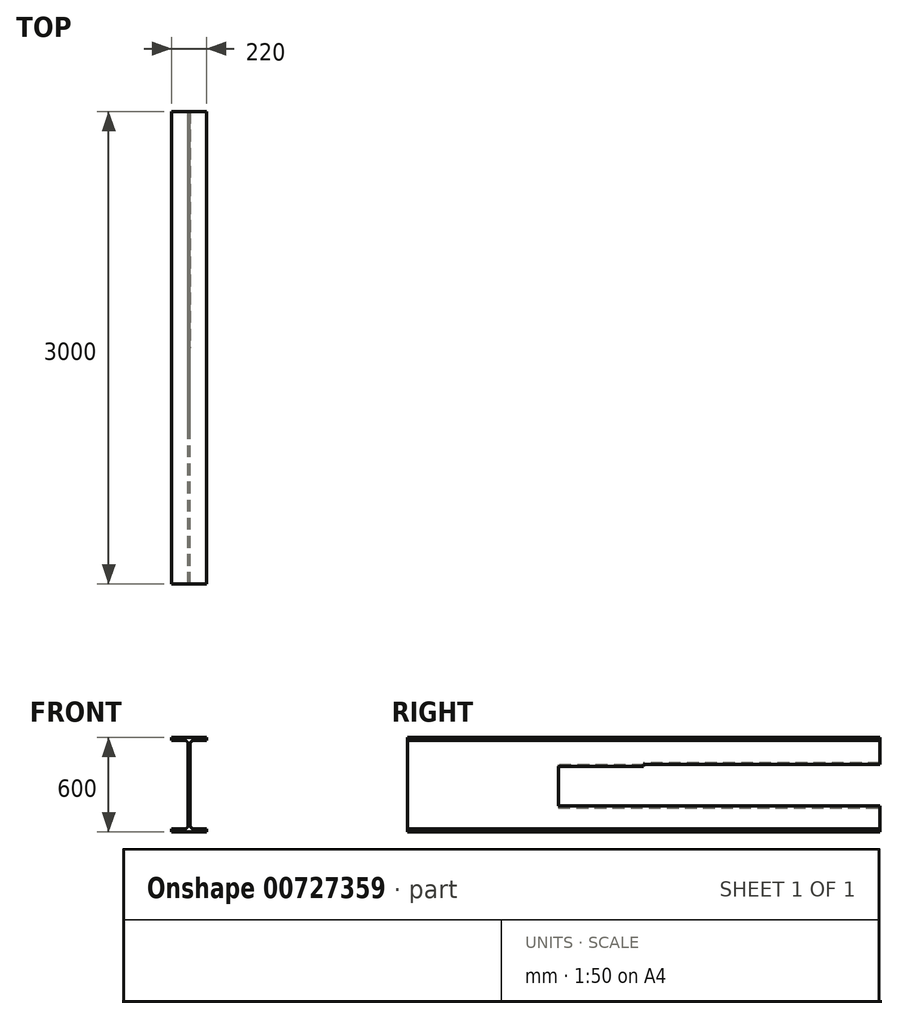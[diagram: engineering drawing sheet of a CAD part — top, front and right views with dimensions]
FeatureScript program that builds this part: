
annotation { "Feature Type Name" : "Feature", "Feature Type Description" : "" }
export const myFeature = defineFeature(function(context is Context, id is Id, definition is map)
    precondition{}
    {
        {
            var Q0;
            Q0=qCreatedBy(makeId("Front.planeOp"),FACE);
            var sketch = newSketch(context, id + "F0", { "sketchPlane" : qUnion([Q0])});
            skLineSegment(sketch, "E0.bottom", {"start": v(-110, 300) * mm, "end": v(110, 300) * mm});
            skLineSegment(sketch, "E0.top", {"start": v(-110, 281) * mm, "end": v(-30, 281) * mm});
            skLineSegment(sketch, "E0.left", {"start": v(-110, 300) * mm, "end": v(-110, 281) * mm});
            skLineSegment(sketch, "E0.right", {"start": v(110, 300) * mm, "end": v(110, 281) * mm});
            skLineSegment(sketch, "E1.top", {"start": v(-6, 0) * mm, "end": v(6, 0) * mm, "construction": true});
            skLineSegment(sketch, "E1.left", {"start": v(-6, 257) * mm, "end": v(-6, 0) * mm});
            skLineSegment(sketch, "E1.right", {"start": v(6, 257) * mm, "end": v(6, 0) * mm});
            skLineSegment(sketch, "E2.trimOffspring", {"start": v(30, 281) * mm, "end": v(110, 281) * mm});
            skPoint(sketch, "E3.visualSharp", {"position": v(-6, 281) * mm});
            skArc(sketch, "E3.filletArc", {"start": v(-6, 257) * mm, "mid": v(-13.03, 273.97) * mm, "end": v(-30, 281) * mm});
            skPoint(sketch, "E4.visualSharp", {"position": v(6, 281) * mm});
            skArc(sketch, "E4.filletArc", {"start": v(30, 281) * mm, "mid": v(13.03, 273.97) * mm, "end": v(6, 257) * mm});
            skLineSegment(sketch, "E5.MirrorCS", {"start": v(-110, -300) * mm, "end": v(-110, -281) * mm});
            skLineSegment(sketch, "E6.MirrorCS", {"start": v(110, -300) * mm, "end": v(110, -281) * mm});
            skArc(sketch, "E7.MirrorCS", {"start": v(-6, -257) * mm, "mid": v(-13.03, -273.97) * mm, "end": v(-30, -281) * mm});
            skArc(sketch, "E8.MirrorCS", {"start": v(30, -281) * mm, "mid": v(13.03, -273.97) * mm, "end": v(6, -257) * mm});
            skLineSegment(sketch, "E9.MirrorCS", {"start": v(-110, -281) * mm, "end": v(-30, -281) * mm});
            skLineSegment(sketch, "E10.MirrorCS", {"start": v(-110, -300) * mm, "end": v(110, -300) * mm});
            skPoint(sketch, "E11.MirrorP", {"position": v(6, -281) * mm});
            skLineSegment(sketch, "E12.MirrorCS", {"start": v(30, -281) * mm, "end": v(110, -281) * mm});
            skLineSegment(sketch, "E13.MirrorCS", {"start": v(6, -257) * mm, "end": v(6, 0) * mm});
            skLineSegment(sketch, "E14.MirrorCS", {"start": v(-6, -257) * mm, "end": v(-6, 0) * mm});
            skPoint(sketch, "E15.MirrorP", {"position": v(-6, -281) * mm});
            skSolve(sketch);
        }
        {
            var Q0;
            Q0=makeQuery(id+"F0.imprint","IMPRINT",FACE,{"disambiguationData":[TD([[makeQuery(id+"F0.imprint","IMPRINT",EDGE,{"derivedFrom":sQuery(id+"F0.wireOp",EDGE,"E0.bottom")}),-1.0]])]});
            extrude(context, id + "F1", {"entities" : qUnion([Q0]), "endBound" : BoundingType.SYMMETRIC, "depth" : 3000 * mm, "offsetDistance" : 25 * mm});
        }
        {
            var Q0;
            Q0=qCreatedBy(makeId("Front.planeOp"),FACE);
            var sketch = newSketch(context, id + "F2", { "sketchPlane" : qUnion([Q0])});
            skLineSegment(sketch, "E16", {"start": v(-6, -138.4) * mm, "end": v(6, -130) * mm});
            skLineSegment(sketch, "E17", {"start": v(-8.33, 0) * mm, "end": v(11.63, 0) * mm, "construction": true});
            skLineSegment(sketch, "E18.MirrorCS", {"start": v(-6, 138.4) * mm, "end": v(6, 130) * mm});
            skLineSegment(sketch, "E19", {"start": v(-6, -138.4) * mm, "end": v(-19.22, -138.4) * mm});
            skLineSegment(sketch, "E20", {"start": v(-19.22, -138.4) * mm, "end": v(-19.22, 138.16) * mm});
            skLineSegment(sketch, "E21", {"start": v(-19.22, 138.16) * mm, "end": v(-6, 138.4) * mm});
            skLineSegment(sketch, "E22", {"start": v(6, 130) * mm, "end": v(18.06, 130) * mm});
            skLineSegment(sketch, "E23", {"start": v(18.06, 130) * mm, "end": v(18.06, -129.68) * mm});
            skLineSegment(sketch, "E24", {"start": v(18.06, -129.68) * mm, "end": v(6, -130) * mm});
            skSolve(sketch);
        }
        {
            var Q0;
            Q0 = qSketchRegion(id + "F2", true);
            extrude(context, id + "F3", {"entities" : qUnion([Q0]), "operationType" : NewBodyOperationType.REMOVE, "oppositeDirection" : true, "depth" : 2800 * mm, "offsetDistance" : 25 * mm});
        }
        {
            var Q0;
            Q0=qCreatedBy(makeId("Right.planeOp"),FACE);
            var sketch = newSketch(context, id + "F4", { "sketchPlane" : qUnion([Q0])});
            skLineSegment(sketch, "E25.bottom", {"start": v(390.64, 114.9) * mm, "end": v(-541.91, 114.9) * mm});
            skLineSegment(sketch, "E25.top", {"start": v(390.64, -134.04) * mm, "end": v(-541.91, -134.04) * mm});
            skLineSegment(sketch, "E25.left", {"start": v(390.64, 114.9) * mm, "end": v(390.64, -134.04) * mm});
            skLineSegment(sketch, "E25.right", {"start": v(-541.91, 114.9) * mm, "end": v(-541.91, -134.04) * mm});
            skSolve(sketch);
        }
        {
            var Q0;
            Q0 = qSketchRegion(id + "F4", true);
            extrude(context, id + "F5", {"entities" : qUnion([Q0]), "operationType" : NewBodyOperationType.REMOVE, "endBound" : BoundingType.THROUGH_ALL, "oppositeDirection" : true, "depth" : 25 * mm, "offsetDistance" : 25 * mm, "hasSecondDirection" : true, "secondDirectionBound" : SecondDirectionBoundingType.THROUGH_ALL, "secondDirectionOppositeDirection" : false, "secondDirectionDepth" : 25 * mm});
        }
        {
            var Q0;
            Q0=makeQuery(id+"F5.boolean.opBoolean","INTERSECT",EDGE,{"derivedFrom":[makeQuery(id+"F1.opExtrude","SWEPT_FACE",FACE,{"disambiguationData":[OSD([sQuery(id+"F0.wireOp",EDGE,"E1.left"),sQuery(id+"F0.wireOp",EDGE,"E14.MirrorCS")])]}),makeQuery(id+"F5.opExtrude","SWEPT_FACE",FACE,{"disambiguationData":[OSD([sQuery(id+"F4.wireOp",EDGE,"E25.bottom")])]})]});
            var Q1;
            Q1=makeQuery(id+"F5.boolean.opBoolean","INTERSECT",EDGE,{"derivedFrom":[makeQuery(id+"F1.opExtrude","SWEPT_FACE",FACE,{"disambiguationData":[OSD([sQuery(id+"F0.wireOp",EDGE,"E1.left"),sQuery(id+"F0.wireOp",EDGE,"E14.MirrorCS")])]}),makeQuery(id+"F5.opExtrude","SWEPT_FACE",FACE,{"disambiguationData":[OSD([sQuery(id+"F4.wireOp",EDGE,"E25.top")])]})]});
            chamfer(context, id + "F6", {"entities" : qUnion([Q0, Q1]), "width" : 12 * mm, "tangentPropagation" : true});
        }
    });
